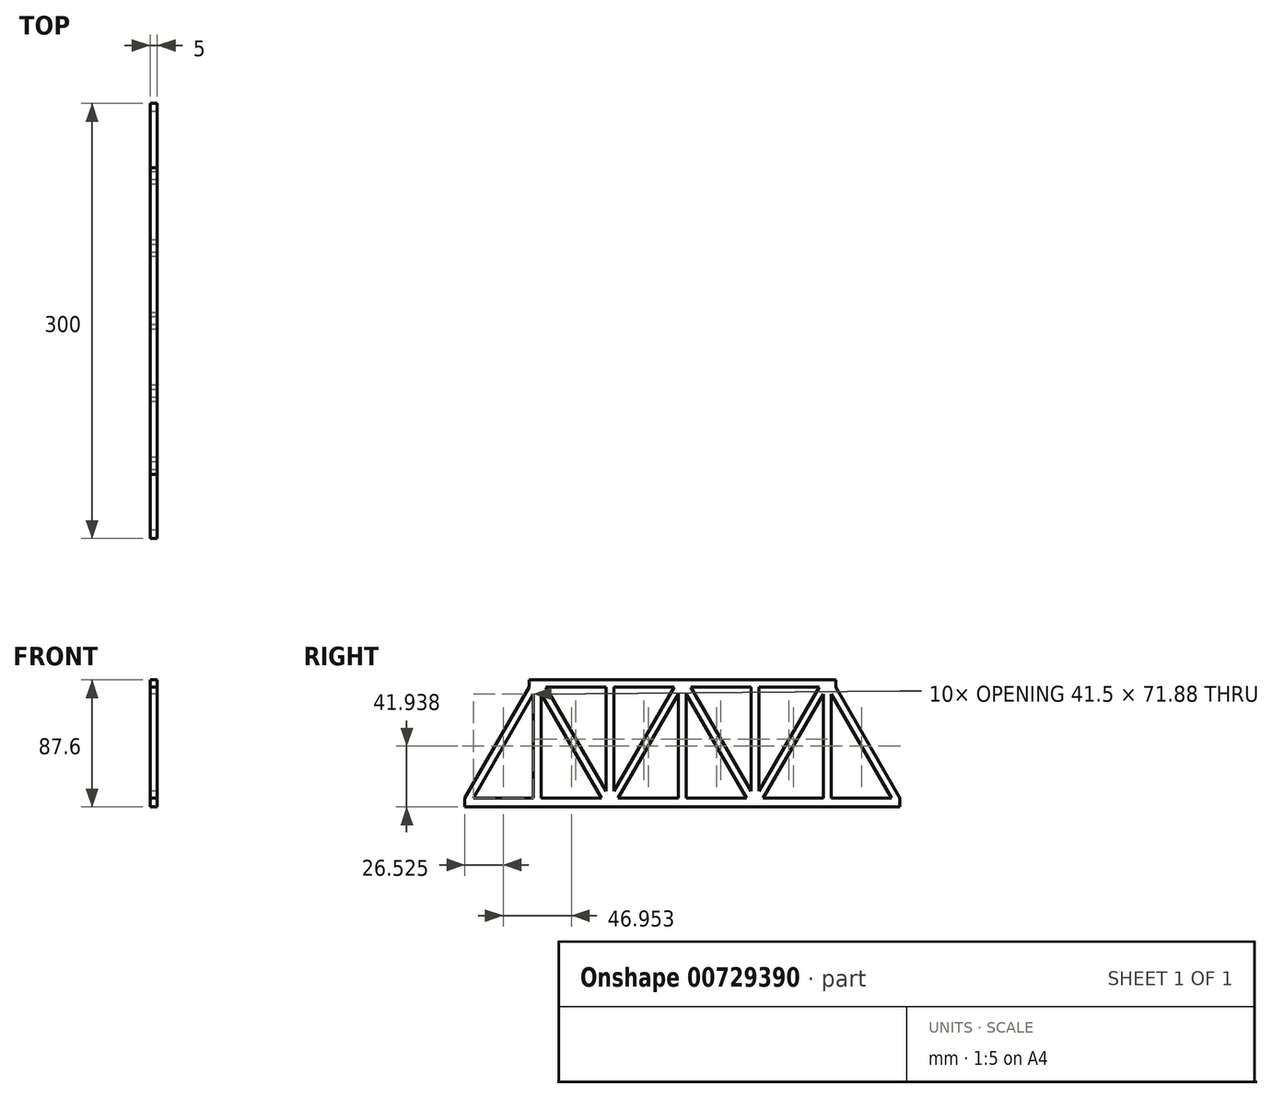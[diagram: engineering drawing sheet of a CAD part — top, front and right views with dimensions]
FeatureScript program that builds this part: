
annotation { "Feature Type Name" : "Feature", "Feature Type Description" : "" }
export const myFeature = defineFeature(function(context is Context, id is Id, definition is map)
    precondition{}
    {
        {
            var Q0;
            Q0=qCreatedBy(makeId("Right.planeOp"),FACE);
            var sketch = newSketch(context, id + "F0", { "sketchPlane" : qUnion([Q0])});
            skLineSegment(sketch, "E0.bottom", {"start": v(154.41, -41.76) * mm, "end": v(-145.59, -41.76) * mm});
            skLineSegment(sketch, "E0.top", {"start": v(154.41, -35.76) * mm, "end": v(-145.59, -35.76) * mm});
            skLineSegment(sketch, "E0.left", {"start": v(154.41, -41.76) * mm, "end": v(154.41, -35.76) * mm});
            skLineSegment(sketch, "E0.right", {"start": v(-145.59, -41.76) * mm, "end": v(-145.59, -35.76) * mm});
            skPoint(sketch, "E0.middle", {"position": v(4.41, -38.76) * mm});
            skLineSegment(sketch, "E1", {"start": v(10.19, 40.84) * mm, "end": v(54.41, -35.76) * mm});
            skLineSegment(sketch, "E2", {"start": v(-139.81, -35.76) * mm, "end": v(-95.59, 40.84) * mm});
            skLineSegment(sketch, "E3", {"start": v(-95.59, 40.84) * mm, "end": v(-51.36, -35.76) * mm});
            skLineSegment(sketch, "E4", {"start": v(-145.59, -35.76) * mm, "end": v(-101.36, 40.84) * mm});
            skLineSegment(sketch, "E5", {"start": v(-45.59, -35.76) * mm, "end": v(-89.81, 40.84) * mm});
            skLineSegment(sketch, "E6", {"start": v(-39.81, -35.76) * mm, "end": v(4.41, 40.84) * mm});
            skPoint(sketch, "E6.endSnap0", {"position": v(4.41, -35.76) * mm});
            skLineSegment(sketch, "E7", {"start": v(4.41, 40.84) * mm, "end": v(48.64, -35.76) * mm});
            skLineSegment(sketch, "E8", {"start": v(-45.59, -35.76) * mm, "end": v(-1.36, 40.84) * mm});
            skLineSegment(sketch, "E9", {"start": v(60.19, -35.76) * mm, "end": v(104.41, 40.84) * mm});
            skLineSegment(sketch, "E10", {"start": v(104.41, 40.84) * mm, "end": v(148.64, -35.76) * mm});
            skLineSegment(sketch, "E11", {"start": v(54.41, -35.76) * mm, "end": v(98.64, 40.84) * mm});
            skLineSegment(sketch, "E12", {"start": v(154.41, -35.76) * mm, "end": v(110.19, 40.84) * mm});
            skLineSegment(sketch, "E13", {"start": v(-101.36, 40.84) * mm, "end": v(110.19, 40.84) * mm});
            skLineSegment(sketch, "E14", {"start": v(-101.36, 40.84) * mm, "end": v(-101.36, 45.84) * mm});
            skLineSegment(sketch, "E15", {"start": v(-101.36, 45.84) * mm, "end": v(110.19, 45.84) * mm});
            skLineSegment(sketch, "E16", {"start": v(110.19, 45.84) * mm, "end": v(110.19, 40.84) * mm});
            skLineSegment(sketch, "E17", {"start": v(-98.31, 36.12) * mm, "end": v(-98.31, -35.76) * mm});
            skLineSegment(sketch, "E18", {"start": v(-98.31, -35.76) * mm, "end": v(-92.86, -35.76) * mm});
            skLineSegment(sketch, "E19", {"start": v(-92.86, -35.76) * mm, "end": v(-92.86, 36.12) * mm});
            skLineSegment(sketch, "E20", {"start": v(-48.31, -31.04) * mm, "end": v(-48.31, 40.84) * mm});
            skLineSegment(sketch, "E21", {"start": v(-48.31, 40.84) * mm, "end": v(-42.86, 40.84) * mm});
            skLineSegment(sketch, "E22", {"start": v(-42.86, 40.84) * mm, "end": v(-42.86, -31.04) * mm});
            skLineSegment(sketch, "E23", {"start": v(1.69, 36.12) * mm, "end": v(1.69, -35.76) * mm});
            skLineSegment(sketch, "E24", {"start": v(7.14, 36.12) * mm, "end": v(7.14, -35.76) * mm});
            skLineSegment(sketch, "E25", {"start": v(51.69, 40.84) * mm, "end": v(51.69, -31.04) * mm});
            skLineSegment(sketch, "E26", {"start": v(57.14, 40.84) * mm, "end": v(57.14, -31.04) * mm});
            skLineSegment(sketch, "E27", {"start": v(101.69, 36.12) * mm, "end": v(101.69, -35.76) * mm});
            skLineSegment(sketch, "E28", {"start": v(107.14, -35.76) * mm, "end": v(107.14, 36.12) * mm});
            skSolve(sketch);
        }
        {
            var Q0;
            {var subQ9=sQuery(id+"F0.wireOp",EDGE,"E14");Q0=makeQuery(id+"F0.imprint","IMPRINT",FACE,{"disambiguationData":[TD([[makeQuery(id+"F0.imprint","IMPRINT",EDGE,{"derivedFrom":subQ9}),-1.0]])]});}
            var Q1;
            {var subQ1=sQuery(id+"F0.wireOp",EDGE,"E0.top");var subQ4=sQuery(id+"F0.wireOp",EDGE,"E3");var subQ5=makeQuery(id+"F0.imprint","INTERSECT",VERTEX,{"derivedFrom":[subQ1,subQ4]});Q1=makeQuery(id+"F0.imprint","IMPRINT",FACE,{"disambiguationData":[TD([[makeQuery(id+"F0.imprint","IMPRINT",EDGE,{"disambiguationData":[TD([[subQ5,1.0]])],"derivedFrom":subQ4}),1.0]])]});}
            var Q2;
            {var subQ4=sQuery(id+"F0.wireOp",EDGE,"E17");Q2=makeQuery(id+"F0.imprint","IMPRINT",FACE,{"disambiguationData":[TD([[makeQuery(id+"F0.imprint","IMPRINT",EDGE,{"derivedFrom":subQ4}),1.0]])]});}
            var Q3;
            {var subQ3=sQuery(id+"F0.wireOp",EDGE,"E20");Q3=makeQuery(id+"F0.imprint","IMPRINT",FACE,{"disambiguationData":[TD([[makeQuery(id+"F0.imprint","IMPRINT",EDGE,{"derivedFrom":subQ3}),-1.0]])]});}
            var Q4;
            {var subQ1=sQuery(id+"F0.wireOp",EDGE,"E6");var subQ4=sQuery(id+"F0.wireOp",EDGE,"E0.top");var subQ5=makeQuery(id+"F0.imprint","INTERSECT",VERTEX,{"derivedFrom":[subQ4,subQ1]});Q4=makeQuery(id+"F0.imprint","IMPRINT",FACE,{"disambiguationData":[TD([[makeQuery(id+"F0.imprint","IMPRINT",EDGE,{"disambiguationData":[TD([[subQ5,-1.0]])],"derivedFrom":subQ1}),1.0]])]});}
            var Q5;
            {var subQ0=sQuery(id+"F0.wireOp",EDGE,"E4");Q5=makeQuery(id+"F0.imprint","IMPRINT",FACE,{"disambiguationData":[TD([[makeQuery(id+"F0.imprint","IMPRINT",EDGE,{"derivedFrom":subQ0}),-1.0]])]});}
            var Q6;
            Q6=makeQuery(id+"F0.imprint","IMPRINT",FACE,{"disambiguationData":[TD([[makeQuery(id+"F0.imprint","IMPRINT",EDGE,{"derivedFrom":sQuery(id+"F0.wireOp",EDGE,"E0.bottom")}),-1.0]])]});
            var Q7;
            {var subQ0=sQuery(id+"F0.wireOp",EDGE,"E23");Q7=makeQuery(id+"F0.imprint","IMPRINT",FACE,{"disambiguationData":[TD([[makeQuery(id+"F0.imprint","IMPRINT",EDGE,{"derivedFrom":subQ0}),1.0]])]});}
            var Q8;
            {var subQ0=sQuery(id+"F0.wireOp",EDGE,"E13");var subQ4=sQuery(id+"F0.wireOp",EDGE,"E1");var subQ5=makeQuery(id+"F0.imprint","INTERSECT",VERTEX,{"derivedFrom":[subQ4,subQ0]});Q8=makeQuery(id+"F0.imprint","IMPRINT",FACE,{"disambiguationData":[TD([[makeQuery(id+"F0.imprint","IMPRINT",EDGE,{"disambiguationData":[TD([[subQ5,-1.0]])],"derivedFrom":subQ4}),-1.0]])]});}
            var Q9;
            {var subQ0=sQuery(id+"F0.wireOp",EDGE,"E25");Q9=makeQuery(id+"F0.imprint","IMPRINT",FACE,{"disambiguationData":[TD([[makeQuery(id+"F0.imprint","IMPRINT",EDGE,{"derivedFrom":subQ0}),1.0]])]});}
            var Q10;
            {var subQ1=sQuery(id+"F0.wireOp",EDGE,"E0.top");var subQ5=sQuery(id+"F0.wireOp",EDGE,"E9");var subQ8=makeQuery(id+"F0.imprint","INTERSECT",VERTEX,{"derivedFrom":[subQ1,subQ5]});Q10=makeQuery(id+"F0.imprint","IMPRINT",FACE,{"disambiguationData":[TD([[makeQuery(id+"F0.imprint","IMPRINT",EDGE,{"disambiguationData":[TD([[subQ8,-1.0]])],"derivedFrom":subQ5}),1.0]])]});}
            var Q11;
            {var subQ4=sQuery(id+"F0.wireOp",EDGE,"E27");Q11=makeQuery(id+"F0.imprint","IMPRINT",FACE,{"disambiguationData":[TD([[makeQuery(id+"F0.imprint","IMPRINT",EDGE,{"derivedFrom":subQ4}),1.0]])]});}
            var Q12;
            {var subQ0=sQuery(id+"F0.wireOp",EDGE,"E12");Q12=makeQuery(id+"F0.imprint","IMPRINT",FACE,{"disambiguationData":[TD([[makeQuery(id+"F0.imprint","IMPRINT",EDGE,{"derivedFrom":subQ0}),1.0]])]});}
            extrude(context, id + "F1", {"entities" : qUnion([Q0, Q1, Q2, Q3, Q4, Q5, Q6, Q7, Q8, Q9, Q10, Q11, Q12]), "depth" : 5 * mm, "offsetDistance" : 25 * mm});
        }
    });
